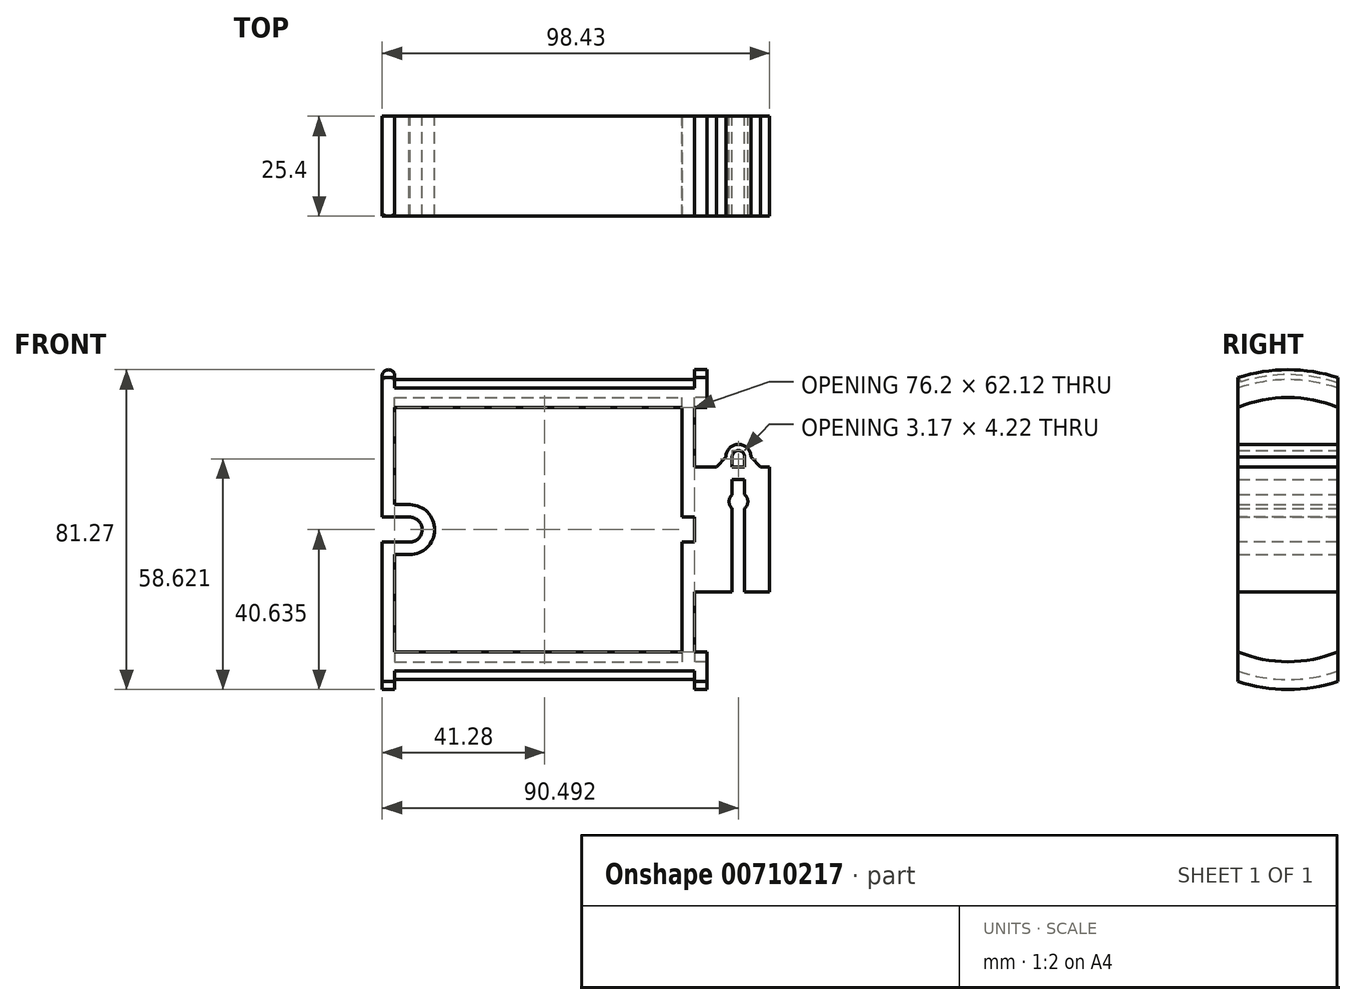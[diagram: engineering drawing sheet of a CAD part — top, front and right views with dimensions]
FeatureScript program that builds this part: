
annotation { "Feature Type Name" : "Feature", "Feature Type Description" : "" }
export const myFeature = defineFeature(function(context is Context, id is Id, definition is map)
    precondition{}
    {
        {
            var Q0;
            Q0=qCreatedBy(makeId("Front.planeOp"),FACE);
            var sketch = newSketch(context, id + "F0", { "sketchPlane" : qUnion([Q0])});
            skLineSegment(sketch, "E0", {"start": v(0, 0) * mm, "end": v(5.56, 0) * mm});
            skLineSegment(sketch, "E1", {"start": v(19.05, 0) * mm, "end": v(19.05, -31.75) * mm});
            skLineSegment(sketch, "E2", {"start": v(19.05, -31.75) * mm, "end": v(12.7, -31.75) * mm});
            skLineSegment(sketch, "E3", {"start": v(12.7, -31.75) * mm, "end": v(12.7, -10.5) * mm});
            skLineSegment(sketch, "E4", {"start": v(12.7, -3.17) * mm, "end": v(9.52, -3.17) * mm});
            skLineSegment(sketch, "E5", {"start": v(9.52, -3.17) * mm, "end": v(9.52, -6.96) * mm});
            skLineSegment(sketch, "E6", {"start": v(9.52, -31.75) * mm, "end": v(0, -31.75) * mm});
            skLineSegment(sketch, "E7", {"start": v(0, 0) * mm, "end": v(0, -31.75) * mm});
            skLineSegment(sketch, "E8", {"start": v(12.7, -3.17) * mm, "end": v(12.7, -6.35) * mm});
            skLineSegment(sketch, "E9", {"start": v(12.7, -31.75) * mm, "end": v(12.7, -28.57) * mm});
            skArc(sketch, "E10", {"start": v(9.52, -6.96) * mm, "mid": v(8.73, -8.73) * mm, "end": v(9.52, -10.5) * mm});
            skArc(sketch, "E11.trimOffspring", {"start": v(12.7, -10.5) * mm, "mid": v(13.5, -8.73) * mm, "end": v(12.7, -6.96) * mm});
            skLineSegment(sketch, "E12.trimOffspring", {"start": v(12.7, -6.96) * mm, "end": v(12.7, -3.17) * mm});
            skLineSegment(sketch, "E13.trimOffspring", {"start": v(9.52, -10.5) * mm, "end": v(9.52, -31.75) * mm});
            skLineSegment(sketch, "E14", {"start": v(11.11, -3.17) * mm, "end": v(11.11, 2.63) * mm});
            skArc(sketch, "E15", {"start": v(12.7, 2.63) * mm, "mid": v(11.11, 4.22) * mm, "end": v(9.52, 2.63) * mm});
            skArc(sketch, "E16", {"start": v(14.29, 2.63) * mm, "mid": v(11.11, 5.8) * mm, "end": v(7.94, 2.63) * mm});
            skLineSegment(sketch, "E17", {"start": v(12.7, 2.63) * mm, "end": v(12.7, 0) * mm});
            skLineSegment(sketch, "E18.trimOffspring", {"start": v(16.67, 0) * mm, "end": v(19.05, 0) * mm});
            skLineSegment(sketch, "E19.MirrorCS", {"start": v(9.52, 2.63) * mm, "end": v(9.52, 0) * mm});
            skLineSegment(sketch, "E20.trimOffspring", {"start": v(9.52, 0) * mm, "end": v(12.7, 0) * mm});
            skLineSegment(sketch, "E21", {"start": v(14.29, 2.63) * mm, "end": v(16.67, 0) * mm});
            skPoint(sketch, "E22.end.orphan", {"position": v(14.29, 0) * mm});
            skLineSegment(sketch, "E23.MirrorCS", {"start": v(7.94, 2.63) * mm, "end": v(5.56, 0) * mm});
            skPoint(sketch, "E24.orphan", {"position": v(7.94, 0) * mm});
            skSolve(sketch);
        }
        {
            var Q0;
            Q0 = qSketchRegion(id + "F0", true);
            extrude(context, id + "F1", {"entities" : qUnion([Q0]), "depth" : 25.4 * mm, "offsetDistance" : 25.4 * mm});
        }
        {
            var Q0;
            Q0=makeQuery(id+"F1.opExtrude","SWEPT_FACE",FACE,{"disambiguationData":[OSD([sQuery(id+"F0.wireOp",EDGE,"E7")])]});
            var sketch = newSketch(context, id + "F2", { "sketchPlane" : qUnion([Q0])});
            skArc(sketch, "E25", {"start": v(0, -51.8) * mm, "mid": v(12.7, -53.98) * mm, "end": v(25.4, -51.8) * mm});
            skLineSegment(sketch, "E26", {"start": v(0, 22.73) * mm, "end": v(0, -54.48) * mm});
            skLineSegment(sketch, "E27", {"start": v(25.4, 22.73) * mm, "end": v(25.4, -54.48) * mm});
            skArc(sketch, "E28", {"start": v(0, -54.48) * mm, "mid": v(12.7, -56.51) * mm, "end": v(25.4, -54.48) * mm});
            skArc(sketch, "E29", {"start": v(0, -46.94) * mm, "mid": v(12.7, -49.43) * mm, "end": v(25.4, -46.94) * mm});
            skArc(sketch, "E30.trimOffspring", {"start": v(25.4, 15.19) * mm, "mid": v(12.7, 17.68) * mm, "end": v(0, 15.19) * mm});
            skArc(sketch, "E31.trimOffspring", {"start": v(25.4, 20.05) * mm, "mid": v(12.7, 22.23) * mm, "end": v(0, 20.05) * mm});
            skArc(sketch, "E32.trimOffspring", {"start": v(25.4, 22.73) * mm, "mid": v(12.7, 24.76) * mm, "end": v(0, 22.73) * mm});
            skLineSegment(sketch, "E33", {"start": v(0, -15.88) * mm, "end": v(0, -12.7) * mm});
            skLineSegment(sketch, "E34", {"start": v(0, -12.7) * mm, "end": v(25.4, -12.7) * mm});
            skLineSegment(sketch, "E35.MirrorCS", {"start": v(0, -19.05) * mm, "end": v(25.4, -19.05) * mm});
            skSolve(sketch);
        }
        {
            var Q0;
            {var subQ0=sQuery(id+"F2.wireOp",EDGE,"E30.trimOffspring");Q0=makeQuery(id+"F2.imprint","IMPRINT",FACE,{"disambiguationData":[TD([[makeQuery(id+"F2.imprint","IMPRINT",EDGE,{"derivedFrom":subQ0}),-1.0]])]});}
            var Q1;
            {var subQ2=sQuery(id+"F2.wireOp",EDGE,"E30.trimOffspring");Q1=makeQuery(id+"F2.imprint","IMPRINT",FACE,{"disambiguationData":[TD([[makeQuery(id+"F2.imprint","IMPRINT",EDGE,{"derivedFrom":subQ2}),1.0]])]});}
            var Q2;
            {var subQ0=sQuery(id+"F2.wireOp",EDGE,"fjNaBxpb-RslY-sPTF-UPwp-iIwQ21hh2yXj");Q2=makeQuery(id+"F2.imprint","IMPRINT",FACE,{"disambiguationData":[TD([[makeQuery(id+"F2.imprint","IMPRINT",EDGE,{"derivedFrom":subQ0}),1.0]])]});}
            var Q3;
            {var subQ0=sQuery(id+"F2.wireOp",EDGE,"fjNaBxpb-RslY-sPTF-UPwp-iIwQ21hh2yXj");Q3=makeQuery(id+"F2.imprint","IMPRINT",FACE,{"disambiguationData":[TD([[makeQuery(id+"F2.imprint","IMPRINT",EDGE,{"derivedFrom":subQ0}),-1.0]])]});}
            var Q4;
            {var subQ2=sQuery(id+"F2.wireOp",EDGE,"E29");Q4=makeQuery(id+"F2.imprint","IMPRINT",FACE,{"disambiguationData":[TD([[makeQuery(id+"F2.imprint","IMPRINT",EDGE,{"derivedFrom":subQ2}),1.0]])]});}
            var Q5;
            {var subQ0=sQuery(id+"F2.wireOp",EDGE,"E25");Q5=makeQuery(id+"F2.imprint","IMPRINT",FACE,{"disambiguationData":[TD([[makeQuery(id+"F2.imprint","IMPRINT",EDGE,{"derivedFrom":subQ0}),1.0]])]});}
            var Q6;
            {var subQ2=sQuery(id+"F2.wireOp",EDGE,"E35.MirrorCS");Q6=makeQuery(id+"F2.imprint","IMPRINT",FACE,{"disambiguationData":[TD([[makeQuery(id+"F2.imprint","IMPRINT",EDGE,{"derivedFrom":subQ2}),-1.0]])]});}
            var Q7;
            {var subQ2=sQuery(id+"F2.wireOp",EDGE,"E34");Q7=makeQuery(id+"F2.imprint","IMPRINT",FACE,{"disambiguationData":[TD([[makeQuery(id+"F2.imprint","IMPRINT",EDGE,{"derivedFrom":subQ2}),1.0]])]});}
            var Q8;
            {var subQ0=sQuery(id+"F2.wireOp",EDGE,"E33");Q8=makeQuery(id+"F2.imprint","IMPRINT",FACE,{"disambiguationData":[TD([[makeQuery(id+"F2.imprint","IMPRINT",EDGE,{"derivedFrom":subQ0}),1.0]])]});}
            extrude(context, id + "F3", {"entities" : qUnion([Q0, Q1, Q2, Q3, Q4, Q5, Q6, Q7, Q8]), "operationType" : NewBodyOperationType.ADD, "depth" : 3.17 * mm, "offsetDistance" : 25.4 * mm});
        }
        {
            var Q0;
            {var subQ0=sQuery(id+"F2.wireOp",EDGE,"E30.trimOffspring");Q0=makeQuery(id+"F2.imprint","IMPRINT",FACE,{"disambiguationData":[TD([[makeQuery(id+"F2.imprint","IMPRINT",EDGE,{"derivedFrom":subQ0}),-1.0]])]});}
            var Q1;
            {var subQ0=sQuery(id+"F2.wireOp",EDGE,"E25");Q1=makeQuery(id+"F2.imprint","IMPRINT",FACE,{"disambiguationData":[TD([[makeQuery(id+"F2.imprint","IMPRINT",EDGE,{"derivedFrom":subQ0}),1.0]])]});}
            extrude(context, id + "F4", {"entities" : qUnion([Q0, Q1]), "operationType" : NewBodyOperationType.ADD, "depth" : 76.2 * mm, "offsetDistance" : 25.4 * mm});
        }
        {
            var Q0;
            {var subQ0=sQuery(id+"F2.wireOp",EDGE,"E25");Q0=makeQuery(id+"F2.imprint","IMPRINT",FACE,{"disambiguationData":[TD([[makeQuery(id+"F2.imprint","IMPRINT",EDGE,{"derivedFrom":subQ0}),-1.0]])]});}
            var Q1;
            {var subQ0=sQuery(id+"F2.wireOp",EDGE,"E25");Q1=makeQuery(id+"F2.imprint","IMPRINT",FACE,{"disambiguationData":[TD([[makeQuery(id+"F2.imprint","IMPRINT",EDGE,{"derivedFrom":subQ0}),1.0]])]});}
            var Q2;
            {var subQ2=sQuery(id+"F2.wireOp",EDGE,"E29");Q2=makeQuery(id+"F2.imprint","IMPRINT",FACE,{"disambiguationData":[TD([[makeQuery(id+"F2.imprint","IMPRINT",EDGE,{"derivedFrom":subQ2}),1.0]])]});}
            var Q3;
            {var subQ2=sQuery(id+"F2.wireOp",EDGE,"E35.MirrorCS");Q3=makeQuery(id+"F2.imprint","IMPRINT",FACE,{"disambiguationData":[TD([[makeQuery(id+"F2.imprint","IMPRINT",EDGE,{"derivedFrom":subQ2}),-1.0]])]});}
            var Q4;
            {var subQ2=sQuery(id+"F2.wireOp",EDGE,"E34");Q4=makeQuery(id+"F2.imprint","IMPRINT",FACE,{"disambiguationData":[TD([[makeQuery(id+"F2.imprint","IMPRINT",EDGE,{"derivedFrom":subQ2}),1.0]])]});}
            var Q5;
            {var subQ2=sQuery(id+"F2.wireOp",EDGE,"E30.trimOffspring");Q5=makeQuery(id+"F2.imprint","IMPRINT",FACE,{"disambiguationData":[TD([[makeQuery(id+"F2.imprint","IMPRINT",EDGE,{"derivedFrom":subQ2}),1.0]])]});}
            var Q6;
            {var subQ0=sQuery(id+"F2.wireOp",EDGE,"E30.trimOffspring");Q6=makeQuery(id+"F2.imprint","IMPRINT",FACE,{"disambiguationData":[TD([[makeQuery(id+"F2.imprint","IMPRINT",EDGE,{"derivedFrom":subQ0}),-1.0]])]});}
            var Q7;
            {var subQ2=sQuery(id+"F2.wireOp",EDGE,"E31.trimOffspring");Q7=makeQuery(id+"F2.imprint","IMPRINT",FACE,{"disambiguationData":[TD([[makeQuery(id+"F2.imprint","IMPRINT",EDGE,{"derivedFrom":subQ2}),-1.0]])]});}
            extrude(context, id + "F5", {"entities" : qUnion([Q0, Q1, Q2, Q3, Q4, Q5, Q6, Q7]), "operationType" : NewBodyOperationType.ADD, "depth" : 79.38 * mm, "offsetDistance" : 25.4 * mm, "hasSecondDirection" : true, "secondDirectionOppositeDirection" : false, "secondDirectionDepth" : 76.2 * mm});
        }
        {
            var Q0;
            {var subQ2=sQuery(id+"F2.wireOp",EDGE,"E31.trimOffspring");Q0=makeQuery(id+"F2.imprint","IMPRINT",FACE,{"disambiguationData":[TD([[makeQuery(id+"F2.imprint","IMPRINT",EDGE,{"derivedFrom":subQ2}),-1.0]])]});}
            var Q1;
            {var subQ0=sQuery(id+"F2.wireOp",EDGE,"E30.trimOffspring");Q1=makeQuery(id+"F2.imprint","IMPRINT",FACE,{"disambiguationData":[TD([[makeQuery(id+"F2.imprint","IMPRINT",EDGE,{"derivedFrom":subQ0}),-1.0]])]});}
            var Q2;
            {var subQ0=sQuery(id+"F2.wireOp",EDGE,"E25");Q2=makeQuery(id+"F2.imprint","IMPRINT",FACE,{"disambiguationData":[TD([[makeQuery(id+"F2.imprint","IMPRINT",EDGE,{"derivedFrom":subQ0}),1.0]])]});}
            var Q3;
            {var subQ0=sQuery(id+"F2.wireOp",EDGE,"E25");Q3=makeQuery(id+"F2.imprint","IMPRINT",FACE,{"disambiguationData":[TD([[makeQuery(id+"F2.imprint","IMPRINT",EDGE,{"derivedFrom":subQ0}),-1.0]])]});}
            extrude(context, id + "F6", {"entities" : qUnion([Q0, Q1, Q2, Q3]), "operationType" : NewBodyOperationType.ADD, "oppositeDirection" : true, "depth" : 3.17 * mm, "offsetDistance" : 25.4 * mm});
        }
        {
            var Q0;
            {var subQ0=sQuery(id+"F2.wireOp",EDGE,"E26");var subQ1=makeQuery(id+"F2.imprint","INTERSECT",VERTEX,{"derivedFrom":[sQuery(id+"F2.wireOp",EDGE,"E25"),subQ0]});var subQ2=makeQuery(id+"F2.imprint","IMPRINT",EDGE,{"disambiguationData":[TD([[subQ1,-1.0]])],"derivedFrom":subQ0});var subQ3=makeQuery(id+"F2.imprint","INTERSECT",VERTEX,{"derivedFrom":[subQ0,sQuery(id+"F2.wireOp",EDGE,"E29")]});var subQ4=makeQuery(id+"F2.imprint","IMPRINT",EDGE,{"disambiguationData":[TD([[subQ1,1.0]])],"derivedFrom":subQ0});var subQ5=makeQuery(id+"F2.imprint","INTERSECT",VERTEX,{"derivedFrom":[subQ0,sQuery(id+"F2.wireOp",EDGE,"E30.trimOffspring")]});var subQ7=makeQuery(id+"F2.imprint","IMPRINT",EDGE,{"disambiguationData":[TD([[subQ5,1.0]])],"derivedFrom":subQ0});var subQ8=makeQuery(id+"F2.imprint","IMPRINT",EDGE,{"disambiguationData":[TD([[makeQuery(id+"F2.imprint","INTERSECT",VERTEX,{"derivedFrom":[subQ0,sQuery(id+"F2.wireOp",EDGE,"E32.trimOffspring")]}),-1.0]])],"derivedFrom":subQ0});var subQ9=sQuery(id+"F0.wireOp",EDGE,"E7");var subQ10=sQuery(id+"F0.wireOp",EDGE,"E6");var subQ12=sQuery(id+"F0.wireOp",EDGE,"E0");var subQ13=makeQuery(id+"F2.imprint","INTERSECT",VERTEX,{"derivedFrom":[makeQuery(id+"F1.opExtrude","SWEPT_EDGE",EDGE,{"disambiguationData":[OSD([subQ12,subQ9])]}),subQ0]});var subQ14=sQuery(id+"F2.wireOp",EDGE,"E33");Q0=makeQuery(id+"F6.boolean.opBoolean","MERGE",FACE,{"derivedFrom":[makeQuery(id+"F5.boolean.opBoolean","MERGE",FACE,{"derivedFrom":[makeQuery(id+"F4.boolean.opBoolean","MERGE",FACE,{"derivedFrom":[makeQuery(id+"F3.boolean.opBoolean","MERGE",FACE,{"derivedFrom":[makeQuery(id+"F1.opExtrude","CAP_FACE",FACE,{"disambiguationData":[OSD([subQ12,sQuery(id+"F0.wireOp",EDGE,"E1"),sQuery(id+"F0.wireOp",EDGE,"E2"),sQuery(id+"F0.wireOp",EDGE,"E3"),sQuery(id+"F0.wireOp",EDGE,"E4"),sQuery(id+"F0.wireOp",EDGE,"E5"),subQ10,subQ9,sQuery(id+"F0.wireOp",EDGE,"E9"),sQuery(id+"F0.wireOp",EDGE,"E10"),sQuery(id+"F0.wireOp",EDGE,"E11.trimOffspring"),sQuery(id+"F0.wireOp",EDGE,"E12.trimOffspring"),sQuery(id+"F0.wireOp",EDGE,"E13.trimOffspring")])],"isStart":true}),makeQuery(id+"F3.opExtrude","SWEPT_FACE",FACE,{"disambiguationData":[OSD([subQ0,subQ14])]})]}),makeQuery(id+"F4.opExtrude","SWEPT_FACE",FACE,{"disambiguationData":[OSD([subQ0]),TDD([subQ7])]}),makeQuery(id+"F4.opExtrude","SWEPT_FACE",FACE,{"disambiguationData":[OSD([subQ0]),TDD([subQ4])]})]}),makeQuery(id+"F5.opExtrude","SWEPT_FACE",FACE,{"disambiguationData":[OSD([subQ0]),TDD([subQ8,subQ7,makeQuery(id+"F2.imprint","IMPRINT",EDGE,{"disambiguationData":[TD([[subQ5,-1.0]])],"derivedFrom":subQ0}),makeQuery(id+"F2.imprint","IMPRINT",EDGE,{"disambiguationData":[TD([[subQ13,-1.0]])],"derivedFrom":subQ0})])]}),makeQuery(id+"F5.opExtrude","SWEPT_FACE",FACE,{"disambiguationData":[OSD([subQ0]),TDD([makeQuery(id+"F2.imprint","IMPRINT",EDGE,{"disambiguationData":[TD([[makeQuery(id+"F2.imprint","INTERSECT",VERTEX,{"derivedFrom":[subQ0,sQuery(id+"F2.wireOp",EDGE,"E35.MirrorCS")]}),-1.0]])],"derivedFrom":subQ0}),makeQuery(id+"F2.imprint","IMPRINT",EDGE,{"disambiguationData":[TD([[subQ3,1.0]])],"derivedFrom":subQ0}),subQ4,subQ2])]})]}),makeQuery(id+"F6.opExtrude","SWEPT_FACE",FACE,{"disambiguationData":[OSD([subQ0]),TDD([subQ8,subQ7])]}),makeQuery(id+"F6.opExtrude","SWEPT_FACE",FACE,{"disambiguationData":[OSD([subQ0]),TDD([subQ4,subQ2])]})]});}
            var sketch = newSketch(context, id + "F7", { "sketchPlane" : qUnion([Q0])});
            skArc(sketch, "E36", {"start": v(72.53, -12.7) * mm, "mid": v(69.24, -15.82) * mm, "end": v(72.41, -19.05) * mm});
            skPoint(sketch, "E36.centerSnap0", {"position": v(76.2, -15.88) * mm});
            skArc(sketch, "E37", {"start": v(72.53, -9.53) * mm, "mid": v(66.06, -15.82) * mm, "end": v(72.41, -22.23) * mm});
            skLineSegment(sketch, "E38", {"start": v(72.3, -12.7) * mm, "end": v(76.2, -12.7) * mm});
            skLineSegment(sketch, "E39", {"start": v(72.41, -19.05) * mm, "end": v(76.2, -19.05) * mm});
            skLineSegment(sketch, "E40", {"start": v(72.41, -22.23) * mm, "end": v(76.2, -22.23) * mm});
            skLineSegment(sketch, "E41", {"start": v(72.3, -9.53) * mm, "end": v(76.2, -9.53) * mm});
            skArc(sketch, "E42", {"start": v(79.38, 21.39) * mm, "mid": v(77.79, 22.72) * mm, "end": v(76.2, 21.39) * mm});
            skPoint(sketch, "E42.startSnap0", {"position": v(76.2, 21.39) * mm});
            skLineSegment(sketch, "E43", {"start": v(77.79, 22.73) * mm, "end": v(76.2, 22.73) * mm});
            skLineSegment(sketch, "E44", {"start": v(77.79, 22.73) * mm, "end": v(79.38, 22.73) * mm});
            skLineSegment(sketch, "E45", {"start": v(79.38, 22.73) * mm, "end": v(79.38, 21.39) * mm});
            skLineSegment(sketch, "E46", {"start": v(77.79, -12.7) * mm, "end": v(77.8, -19.05) * mm});
            skLineSegment(sketch, "E47", {"start": v(77.79, -15.88) * mm, "end": v(76.2, -15.88) * mm});
            skSolve(sketch);
        }
        {
            var Q0;
            {var subQ4=sQuery(id+"F7.wireOp",EDGE,"E39");Q0=makeQuery(id+"F7.imprint","IMPRINT",FACE,{"disambiguationData":[TD([[makeQuery(id+"F7.imprint","IMPRINT",EDGE,{"derivedFrom":subQ4}),-1.0]])]});}
            extrude(context, id + "F8", {"entities" : qUnion([Q0]), "operationType" : NewBodyOperationType.ADD, "oppositeDirection" : true, "depth" : 25.4 * mm, "offsetDistance" : 25.4 * mm});
        }
        {
            var Q0;
            {var subQ1=sQuery(id+"F7.wireOp",EDGE,"E42");Q0=makeQuery(id+"F7.imprint","IMPRINT",FACE,{"disambiguationData":[TD([[makeQuery(id+"F7.imprint","IMPRINT",EDGE,{"derivedFrom":subQ1}),-1.0]])]});}
            var Q1;
            Q1=makeQuery(id+"F5.opExtrude","CAP_EDGE",EDGE,{"disambiguationData":[OSD([sQuery(id+"F2.wireOp",EDGE,"E32.trimOffspring")])],"isStart":false});
            sweep(context, id + "F9", {"operationType" : NewBodyOperationType.REMOVE, "profiles" : qUnion([Q0]), "path" : qUnion([Q1])});
        }
    });
